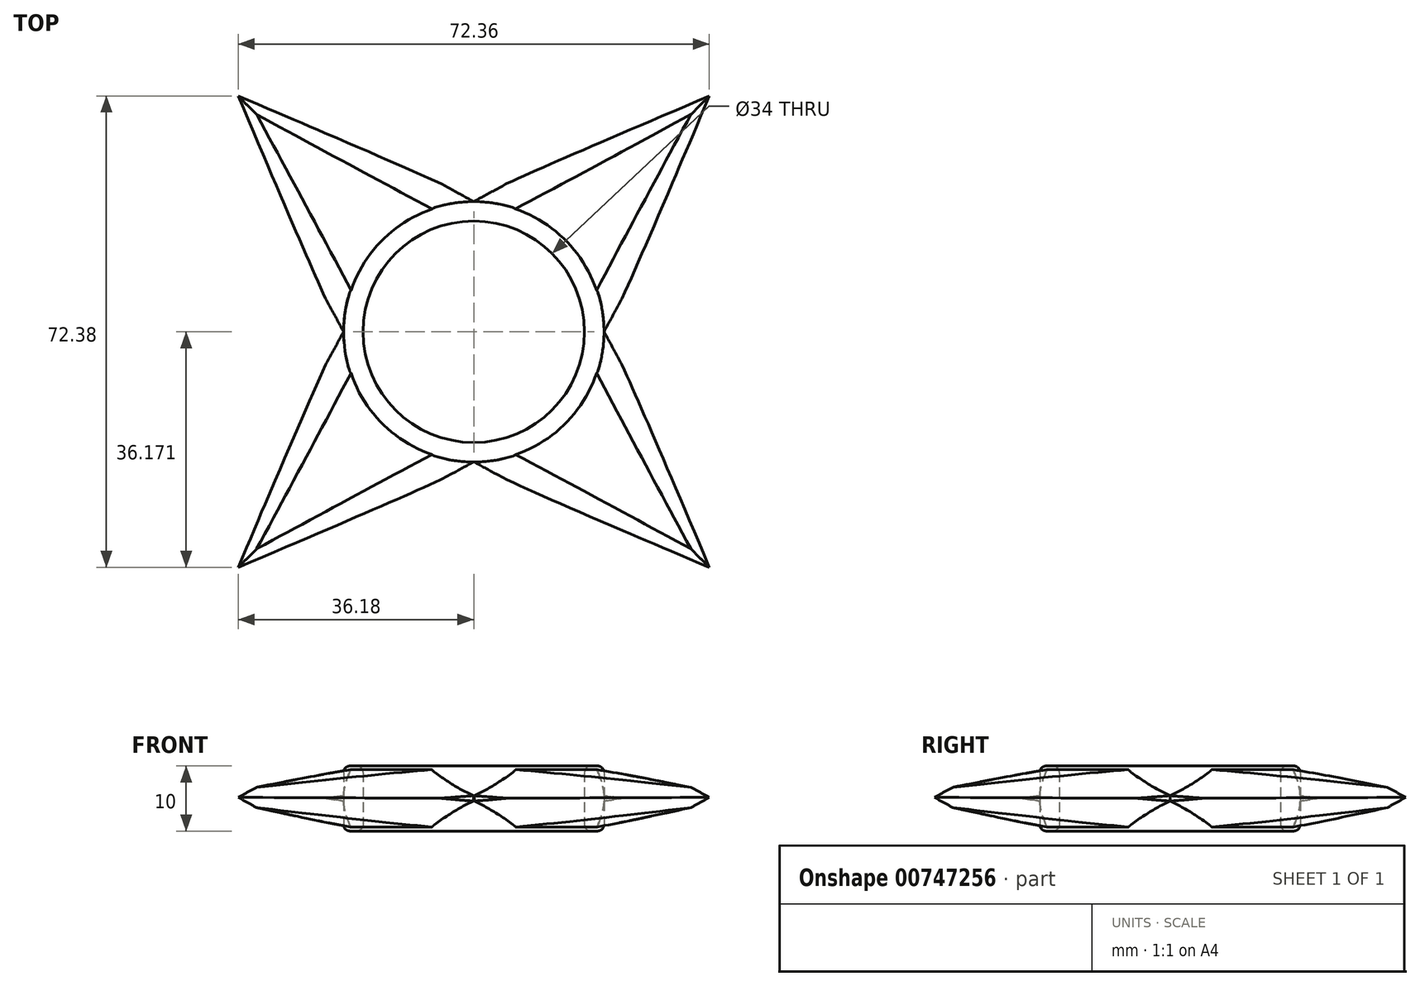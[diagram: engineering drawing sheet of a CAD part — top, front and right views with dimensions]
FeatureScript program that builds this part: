
annotation { "Feature Type Name" : "Feature", "Feature Type Description" : "" }
export const myFeature = defineFeature(function(context is Context, id is Id, definition is map)
    precondition{}
    {
        {
            var Q0;
            Q0=qCreatedBy(makeId("Top.planeOp"),FACE);
            var sketch = newSketch(context, id + "F0", { "sketchPlane" : qUnion([Q0])});
            skLineSegment(sketch, "E0.bottom", {"start": v(0, 19.98) * mm, "end": v(0, 19.98) * mm});
            skLineSegment(sketch, "E0.top", {"start": v(0, 19.98) * mm, "end": v(0, 19.98) * mm});
            skLineSegment(sketch, "E0.left", {"start": v(0, 19.98) * mm, "end": v(0, 19.98) * mm});
            skPoint(sketch, "E1.first.point", {"position": v(-20, 0) * mm});
            skPoint(sketch, "E1.third.point", {"position": v(0, 19.98) * mm});
            skPoint(sketch, "E2.middle", {"position": v(0, 0) * mm});
            skLineSegment(sketch, "E3", {"start": v(-20, 0) * mm, "end": v(-43.9, 43.92) * mm});
            skLineSegment(sketch, "E4", {"start": v(-43.9, 43.92) * mm, "end": v(0, 19.98) * mm});
            skLineSegment(sketch, "E5", {"start": v(0, 19.98) * mm, "end": v(43.9, 43.92) * mm});
            skLineSegment(sketch, "E6", {"start": v(43.9, 43.92) * mm, "end": v(20, 0) * mm});
            skLineSegment(sketch, "E7", {"start": v(20, 0) * mm, "end": v(43.9, -43.92) * mm});
            skLineSegment(sketch, "E8", {"start": v(43.9, -43.92) * mm, "end": v(0, -19.98) * mm});
            skLineSegment(sketch, "E9", {"start": v(0, -19.98) * mm, "end": v(-43.9, -43.92) * mm});
            skLineSegment(sketch, "E10", {"start": v(-43.9, -43.92) * mm, "end": v(-20, 0) * mm});
            skCircle(sketch, "E11", {"center": v(0, -0.02) * mm, "radius": 20 * mm});
            skLineSegment(sketch, "E12.trimOffspring", {"start": v(0.13, -0.15) * mm, "end": v(0, -0.02) * mm});
            skSolve(sketch);
        }
        {
            var Q0;
            Q0 = qSketchRegion(id + "F0", true);
            extrude(context, id + "F1", {"entities" : qUnion([Q0]), "depth" : 10 * mm, "offsetDistance" : 25 * mm});
        }
        {
            var Q0;
            {var subQ0=sQuery(id+"F0.wireOp",EDGE,"E11");var subQ1=makeQuery(id+"F0.imprint","INTERSECT",VERTEX,{"derivedFrom":[sQuery(id+"F0.wireOp",EDGE,"E4"),sQuery(id+"F0.wireOp",EDGE,"E5"),subQ0]});Q0=makeQuery(id+"F0.imprint","IMPRINT",FACE,{"disambiguationData":[TD([[makeQuery(id+"F0.imprint","IMPRINT",EDGE,{"disambiguationData":[TD([[subQ1,1.0]])],"derivedFrom":subQ0}),1.0]])]});}
            extrude(context, id + "F2", {"entities" : qUnion([Q0]), "operationType" : NewBodyOperationType.REMOVE, "depth" : 10.8 * mm, "offsetDistance" : 25 * mm});
        }
        {
            var Q0;
            Q0=qCreatedBy(makeId("Top.planeOp"),FACE);
            var sketch = newSketch(context, id + "F3", { "sketchPlane" : qUnion([Q0])});
            skLineSegment(sketch, "E13", {"start": v(-43.9, -43.92) * mm, "end": v(43.9, 43.92) * mm});
            skSolve(sketch);
        }
        {
            var Q0;
            Q0=sQuery(id+"F3.wireOp",EDGE,"E13");
            extrude(context, id + "F4", {"bodyType" : ToolBodyType.SURFACE, "surfaceEntities" : qUnion([Q0]), "endBound" : BoundingType.SYMMETRIC, "depth" : .1 * mm, "offsetDistance" : 25 * mm});
        }
        {
            var Q0;
            Q0=makeQuery(id+"F4.opExtrude","SWEPT_FACE",FACE,{"disambiguationData":[OSD([sQuery(id+"F3.wireOp",EDGE,"E13")])]});
            var sketch = newSketch(context, id + "F5", { "sketchPlane" : qUnion([Q0])});
            skLineSegment(sketch, "E14", {"start": v(-14.14, 10) * mm, "end": v(-62.1, 5.24) * mm});
            skLineSegment(sketch, "E15", {"start": v(-62.1, 5.24) * mm, "end": v(-14.19, 0) * mm});
            skLineSegment(sketch, "E16", {"start": v(-14.19, 0) * mm, "end": v(-96.74, -8.2) * mm});
            skLineSegment(sketch, "E17", {"start": v(-96.74, -8.2) * mm, "end": v(-96.74, 39.92) * mm});
            skLineSegment(sketch, "E18", {"start": v(-96.74, 39.92) * mm, "end": v(-14.14, 10) * mm});
            skLineSegment(sketch, "E19", {"start": v(0, 31.28) * mm, "end": v(0, -22.7) * mm, "construction": true});
            skPoint(sketch, "E20", {"position": v(-62.1, 5.24) * mm});
            skSolve(sketch);
        }
        {
            var Q0;
            {var subQ0=sQuery(id+"F5.wireOp",EDGE,"E14");Q0=makeQuery(id+"F5.imprint","IMPRINT",FACE,{"disambiguationData":[TD([[makeQuery(id+"F5.imprint","IMPRINT",EDGE,{"derivedFrom":subQ0}),-1.0]])]});}
            var Q1;
            {var subQ5=sQuery(id+"F5.wireOp",EDGE,"E17");Q1=makeQuery(id+"F5.imprint","IMPRINT",FACE,{"disambiguationData":[TD([[makeQuery(id+"F5.imprint","IMPRINT",EDGE,{"derivedFrom":subQ5}),-1.0]])]});}
            var Q2;
            {var subQ0=sQuery(id+"F5.wireOp",EDGE,"E15");Q2=makeQuery(id+"F5.imprint","IMPRINT",FACE,{"disambiguationData":[TD([[makeQuery(id+"F5.imprint","IMPRINT",EDGE,{"derivedFrom":subQ0}),-1.0]])]});}
            var Q3;
            Q3=sQuery(id+"F5.wireOp",EDGE,"E19");
            revolve(context, id + "F6", {"operationType" : NewBodyOperationType.REMOVE, "surfaceOperationType" : NewSurfaceOperationType.NEW, "entities" : qUnion([Q0, Q1, Q2]), "axis" : qUnion([Q3]), "revolveType" : RevolveType.FULL, "oppositeDirection" : true});
        }
        {
            var Q0;
            Q0=makeQuery(id+"F6.boolean.opBoolean","INTERSECT",EDGE,{"derivedFrom":[makeQuery(id+"F1.opExtrude","SWEPT_FACE",FACE,{"disambiguationData":[OSD([sQuery(id+"F0.wireOp",EDGE,"E8")])]}),makeQuery(id+"F6.opRevolve","SWEPT_FACE",FACE,{"disambiguationData":[OSD([sQuery(id+"F5.wireOp",EDGE,"E14")])]})]});
            var Q1;
            Q1=makeQuery(id+"F6.boolean.opBoolean","INTERSECT",EDGE,{"derivedFrom":[makeQuery(id+"F1.opExtrude","SWEPT_FACE",FACE,{"disambiguationData":[OSD([sQuery(id+"F0.wireOp",EDGE,"E8")])]}),makeQuery(id+"F6.opRevolve","SWEPT_FACE",FACE,{"disambiguationData":[OSD([sQuery(id+"F5.wireOp",EDGE,"E15")])]})]});
            chamfer(context, id + "F7", {"entities" : qUnion([Q0, Q1]), "width" : 4.34 * mm, "tangentPropagation" : true});
        }
        {
            var Q0;
            Q0=makeQuery(id+"F6.boolean.opBoolean","INTERSECT",EDGE,{"derivedFrom":[makeQuery(id+"F1.opExtrude","SWEPT_FACE",FACE,{"disambiguationData":[OSD([sQuery(id+"F0.wireOp",EDGE,"E7")])]}),makeQuery(id+"F6.opRevolve","SWEPT_FACE",FACE,{"disambiguationData":[OSD([sQuery(id+"F5.wireOp",EDGE,"E14")])]})]});
            var Q1;
            Q1=makeQuery(id+"F6.boolean.opBoolean","INTERSECT",EDGE,{"derivedFrom":[makeQuery(id+"F1.opExtrude","SWEPT_FACE",FACE,{"disambiguationData":[OSD([sQuery(id+"F0.wireOp",EDGE,"E7")])]}),makeQuery(id+"F6.opRevolve","SWEPT_FACE",FACE,{"disambiguationData":[OSD([sQuery(id+"F5.wireOp",EDGE,"E15")])]})]});
            chamfer(context, id + "F8", {"entities" : qUnion([Q0, Q1]), "width" : 4.34 * mm, "tangentPropagation" : true});
        }
        {
            var Q0;
            Q0=makeQuery(id+"F6.boolean.opBoolean","INTERSECT",EDGE,{"derivedFrom":[makeQuery(id+"F1.opExtrude","SWEPT_FACE",FACE,{"disambiguationData":[OSD([sQuery(id+"F0.wireOp",EDGE,"E6")])]}),makeQuery(id+"F6.opRevolve","SWEPT_FACE",FACE,{"disambiguationData":[OSD([sQuery(id+"F5.wireOp",EDGE,"E14")])]})]});
            var Q1;
            Q1=makeQuery(id+"F6.boolean.opBoolean","INTERSECT",EDGE,{"derivedFrom":[makeQuery(id+"F1.opExtrude","SWEPT_FACE",FACE,{"disambiguationData":[OSD([sQuery(id+"F0.wireOp",EDGE,"E6")])]}),makeQuery(id+"F6.opRevolve","SWEPT_FACE",FACE,{"disambiguationData":[OSD([sQuery(id+"F5.wireOp",EDGE,"E15")])]})]});
            chamfer(context, id + "F9", {"entities" : qUnion([Q0, Q1]), "width" : 4.34 * mm, "tangentPropagation" : true});
        }
        {
            var Q0;
            Q0=makeQuery(id+"F6.boolean.opBoolean","INTERSECT",EDGE,{"derivedFrom":[makeQuery(id+"F1.opExtrude","SWEPT_FACE",FACE,{"disambiguationData":[OSD([sQuery(id+"F0.wireOp",EDGE,"E5")])]}),makeQuery(id+"F6.opRevolve","SWEPT_FACE",FACE,{"disambiguationData":[OSD([sQuery(id+"F5.wireOp",EDGE,"E14")])]})]});
            var Q1;
            Q1=makeQuery(id+"F6.boolean.opBoolean","INTERSECT",EDGE,{"derivedFrom":[makeQuery(id+"F1.opExtrude","SWEPT_FACE",FACE,{"disambiguationData":[OSD([sQuery(id+"F0.wireOp",EDGE,"E5")])]}),makeQuery(id+"F6.opRevolve","SWEPT_FACE",FACE,{"disambiguationData":[OSD([sQuery(id+"F5.wireOp",EDGE,"E15")])]})]});
            chamfer(context, id + "F10", {"entities" : qUnion([Q0, Q1]), "width" : 4.34 * mm, "tangentPropagation" : true});
        }
        {
            var Q0;
            Q0=makeQuery(id+"F6.boolean.opBoolean","INTERSECT",EDGE,{"derivedFrom":[makeQuery(id+"F1.opExtrude","SWEPT_FACE",FACE,{"disambiguationData":[OSD([sQuery(id+"F0.wireOp",EDGE,"E4")])]}),makeQuery(id+"F6.opRevolve","SWEPT_FACE",FACE,{"disambiguationData":[OSD([sQuery(id+"F5.wireOp",EDGE,"E14")])]})]});
            var Q1;
            Q1=makeQuery(id+"F6.boolean.opBoolean","INTERSECT",EDGE,{"derivedFrom":[makeQuery(id+"F1.opExtrude","SWEPT_FACE",FACE,{"disambiguationData":[OSD([sQuery(id+"F0.wireOp",EDGE,"E4")])]}),makeQuery(id+"F6.opRevolve","SWEPT_FACE",FACE,{"disambiguationData":[OSD([sQuery(id+"F5.wireOp",EDGE,"E15")])]})]});
            chamfer(context, id + "F11", {"entities" : qUnion([Q0, Q1]), "width" : 4.35 * mm, "tangentPropagation" : true});
        }
        {
            var Q0;
            Q0=makeQuery(id+"F6.boolean.opBoolean","INTERSECT",EDGE,{"derivedFrom":[makeQuery(id+"F1.opExtrude","SWEPT_FACE",FACE,{"disambiguationData":[OSD([sQuery(id+"F0.wireOp",EDGE,"E3")])]}),makeQuery(id+"F6.opRevolve","SWEPT_FACE",FACE,{"disambiguationData":[OSD([sQuery(id+"F5.wireOp",EDGE,"E15")])]})]});
            var Q1;
            Q1=makeQuery(id+"F6.boolean.opBoolean","INTERSECT",EDGE,{"derivedFrom":[makeQuery(id+"F1.opExtrude","SWEPT_FACE",FACE,{"disambiguationData":[OSD([sQuery(id+"F0.wireOp",EDGE,"E3")])]}),makeQuery(id+"F6.opRevolve","SWEPT_FACE",FACE,{"disambiguationData":[OSD([sQuery(id+"F5.wireOp",EDGE,"E14")])]})]});
            chamfer(context, id + "F12", {"entities" : qUnion([Q0, Q1]), "width" : 4.34 * mm, "tangentPropagation" : true});
        }
        {
            var Q0;
            Q0=makeQuery(id+"F6.boolean.opBoolean","INTERSECT",EDGE,{"derivedFrom":[makeQuery(id+"F1.opExtrude","SWEPT_FACE",FACE,{"disambiguationData":[OSD([sQuery(id+"F0.wireOp",EDGE,"E10")])]}),makeQuery(id+"F6.opRevolve","SWEPT_FACE",FACE,{"disambiguationData":[OSD([sQuery(id+"F5.wireOp",EDGE,"E15")])]})]});
            var Q1;
            Q1=makeQuery(id+"F6.boolean.opBoolean","INTERSECT",EDGE,{"derivedFrom":[makeQuery(id+"F1.opExtrude","SWEPT_FACE",FACE,{"disambiguationData":[OSD([sQuery(id+"F0.wireOp",EDGE,"E10")])]}),makeQuery(id+"F6.opRevolve","SWEPT_FACE",FACE,{"disambiguationData":[OSD([sQuery(id+"F5.wireOp",EDGE,"E14")])]})]});
            chamfer(context, id + "F13", {"entities" : qUnion([Q0, Q1]), "width" : 4.34 * mm, "tangentPropagation" : true});
        }
        {
            var Q0;
            Q0=makeQuery(id+"F6.boolean.opBoolean","INTERSECT",EDGE,{"derivedFrom":[makeQuery(id+"F1.opExtrude","SWEPT_FACE",FACE,{"disambiguationData":[OSD([sQuery(id+"F0.wireOp",EDGE,"E9")])]}),makeQuery(id+"F6.opRevolve","SWEPT_FACE",FACE,{"disambiguationData":[OSD([sQuery(id+"F5.wireOp",EDGE,"E14")])]})]});
            var Q1;
            Q1=makeQuery(id+"F6.boolean.opBoolean","INTERSECT",EDGE,{"derivedFrom":[makeQuery(id+"F1.opExtrude","SWEPT_FACE",FACE,{"disambiguationData":[OSD([sQuery(id+"F0.wireOp",EDGE,"E9")])]}),makeQuery(id+"F6.opRevolve","SWEPT_FACE",FACE,{"disambiguationData":[OSD([sQuery(id+"F5.wireOp",EDGE,"E15")])]})]});
            chamfer(context, id + "F14", {"entities" : qUnion([Q0, Q1]), "width" : 4.34 * mm, "tangentPropagation" : true});
        }
        {
            var Q0;
            Q0=qCreatedBy(makeId("Top.planeOp"),FACE);
            var sketch = newSketch(context, id + "F15", { "sketchPlane" : qUnion([Q0])});
            skCircle(sketch, "E21", {"center": v(0, -0.02) * mm, "radius": 20 * mm});
            skPoint(sketch, "E21.first.point", {"position": v(0, 19.98) * mm});
            skPoint(sketch, "E21.second.point", {"position": v(20, 0) * mm});
            skPoint(sketch, "E21.third.point", {"position": v(-20, 0) * mm});
            skCircle(sketch, "E22", {"center": v(0, -0.02) * mm, "radius": 17 * mm});
            skPoint(sketch, "E23", {"position": v(-17, 0) * mm});
            skPoint(sketch, "E24", {"position": v(0, 16.98) * mm});
            skPoint(sketch, "E25", {"position": v(17, 0) * mm});
            skPoint(sketch, "E26", {"position": v(0, -17.02) * mm});
            skSolve(sketch);
        }
        {
            var Q0;
            Q0=makeQuery(id+"F15.imprint","IMPRINT",FACE,{"disambiguationData":[TD([[makeQuery(id+"F15.imprint","IMPRINT",EDGE,{"derivedFrom":sQuery(id+"F15.wireOp",EDGE,"E21")}),1.0]])]});
            extrude(context, id + "F16", {"entities" : qUnion([Q0]), "operationType" : NewBodyOperationType.ADD, "depth" : 10 * mm, "offsetDistance" : 25 * mm});
        }
        {
            var Q0;
            Q0=makeQuery(id+"F16.opExtrude","CAP_EDGE",EDGE,{"disambiguationData":[OSD([sQuery(id+"F15.wireOp",EDGE,"E22")])],"isStart":false});
            fillet(context, id + "F17", {"entities" : qUnion([Q0]), "radius" : 1 * mm, "tangentPropagation" : true, "allowEdgeOverflow" : false});
        }
        {
            var Q0;
            Q0=makeQuery(id+"F16.opExtrude","CAP_EDGE",EDGE,{"disambiguationData":[OSD([sQuery(id+"F15.wireOp",EDGE,"E21")])],"isStart":false});
            fillet(context, id + "F18", {"entities" : qUnion([Q0]), "radius" : 1 * mm, "tangentPropagation" : true, "allowEdgeOverflow" : false});
        }
        {
            var Q0;
            Q0=makeQuery(id+"F16.opExtrude","CAP_EDGE",EDGE,{"disambiguationData":[OSD([sQuery(id+"F15.wireOp",EDGE,"E22")])],"isStart":true});
            fillet(context, id + "F19", {"entities" : qUnion([Q0]), "radius" : 1 * mm, "tangentPropagation" : true, "allowEdgeOverflow" : false});
        }
        {
            var Q0;
            Q0=makeQuery(id+"F16.opExtrude","CAP_EDGE",EDGE,{"disambiguationData":[OSD([sQuery(id+"F15.wireOp",EDGE,"E21")])],"isStart":true});
            fillet(context, id + "F20", {"entities" : qUnion([Q0]), "radius" : 1 * mm, "tangentPropagation" : true, "allowEdgeOverflow" : false});
        }
    });
